# Revit family: 34-DESAGUE PUSH METAL SIN REBOSE
name_source: partatom
category: Aparatos sanitarios
revit_build: Autodesk Revit 2018 (Build: 20170223_1515(x64)
units: mm (PartAtom-declared; Revit-internal decimal feet)

## family parameters
Anfitrión = Cara
Compartido = No
Corte con vacíos al cargar = No
Cota de conector redondo = Diámetro de uso
Número OmniClass = 23.45.55.21
Punto de cálculo de habitación = No
Tipo de pieza = Normal
Título OmniClass = Drains (Wastes)

## types (1)
- 34-DESAGUE PUSH METAL SIN REBOSE
    Acabado = Brillante
    Altura Nominal = 330
    Ancho Nominal = 40.6
    Características = Resistente al efecto de jabones y limpiadores, resistente a la corrosión
    Color = Cromo
    Cumplimiento de Norma = Ahorro de agua (8,3l/min.) cumple norma NTC 1644
    Código de montaje = D2010
    Descripción = Plumbing Fixtures
    Descripción IFC = Desagüe largo metálico sin rebose
    Elevación por defecto = 0 mm  [stored 0 ft]
    Fabricante = www.corona.com.co
    Forma = Cilindríca
    Logitud Nominal = 64.5
    Material Acabado = Cromo-Corona
    Material de Fabricación = Latón / Recubrimiento cromo (acabados)
    Nombre = Desagüe largo
    Nombre del Fabricante = Corona
    Número Modelo = 935385551
    Requerimientos Accesibilidad = Manual
    Responsable Garantías Partes = www.corona.com.co
    Tamaño = 64,5 x 40,6 x 330
    Tipo de Activo = Fijo
    Tráfico = Residencial

note: [stored X ft] marks values corroborated as IEEE doubles in the binary element streams (Revit-internal decimal feet)

## geometry (parser evidence)
native form markers: Sweep x2
no freeform markers — native parametric forms only
